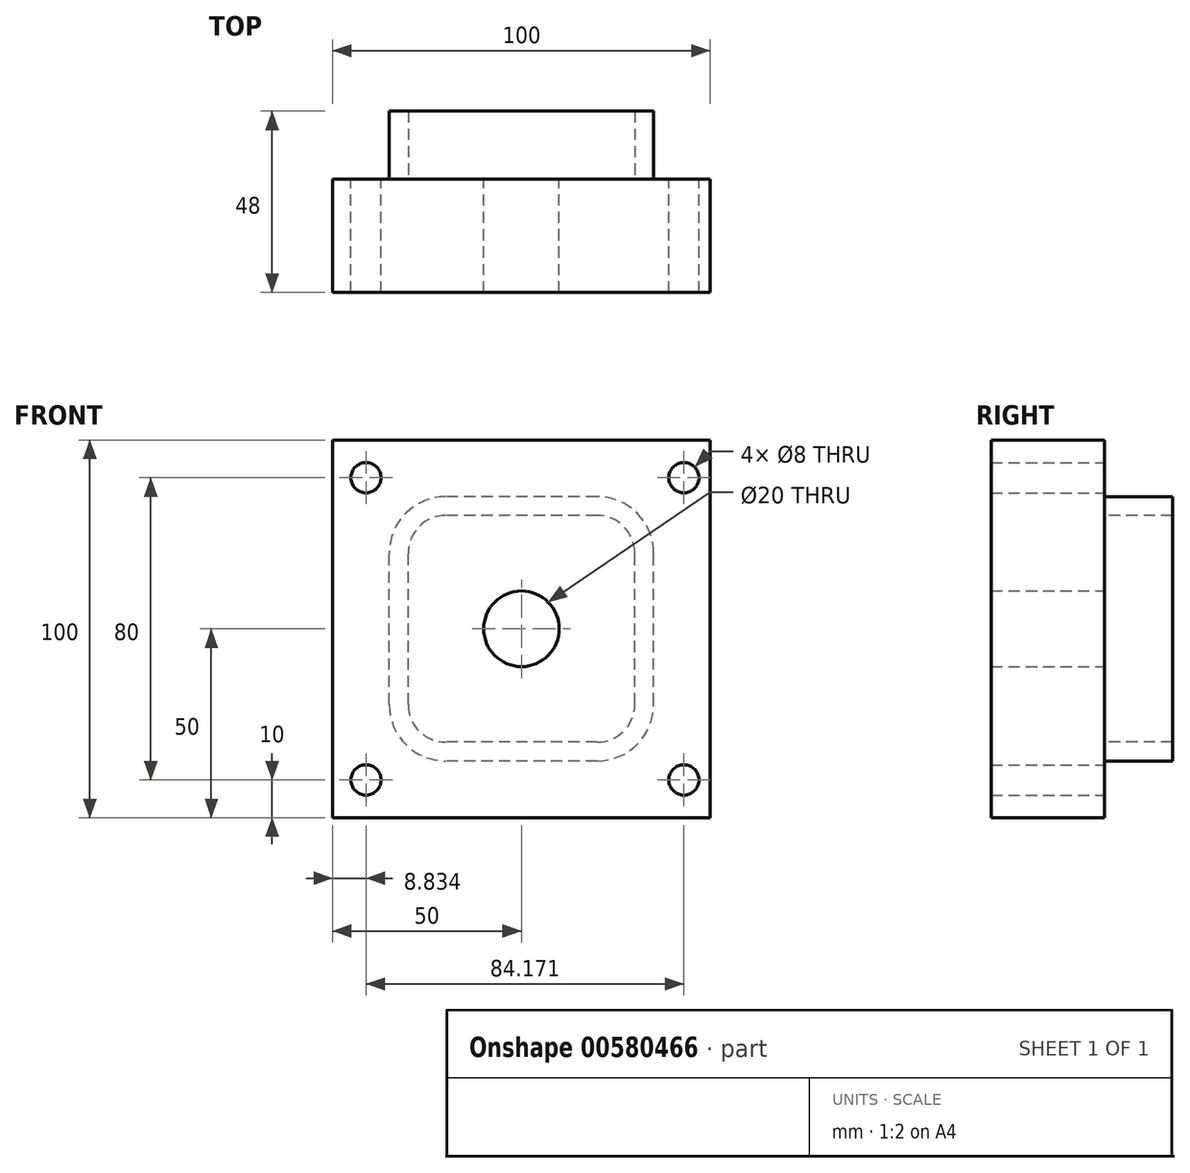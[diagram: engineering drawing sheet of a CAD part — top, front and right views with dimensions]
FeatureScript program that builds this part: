
annotation { "Feature Type Name" : "Feature", "Feature Type Description" : "" }
export const myFeature = defineFeature(function(context is Context, id is Id, definition is map)
    precondition{}
    {
        {
            var Q0;
            Q0=qCreatedBy(makeId("Front.planeOp"),FACE);
            var sketch = newSketch(context, id + "F0", { "sketchPlane" : qUnion([Q0])});
            skLineSegment(sketch, "E0.bottom", {"start": v(50, 0) * mm, "end": v(-50, 0) * mm});
            skLineSegment(sketch, "E0.top", {"start": v(50, -100) * mm, "end": v(-50, -100) * mm});
            skLineSegment(sketch, "E0.left", {"start": v(50, 0) * mm, "end": v(50, -100) * mm});
            skLineSegment(sketch, "E0.right", {"start": v(-50, 0) * mm, "end": v(-50, -100) * mm});
            skSolve(sketch);
        }
        {
            var Q0;
            Q0=makeQuery(id+"F0.imprint","IMPRINT",FACE,{"disambiguationData":[TD([[makeQuery(id+"F0.imprint","IMPRINT",EDGE,{"derivedFrom":sQuery(id+"F0.wireOp",EDGE,"E0.bottom")}),1.0]])]});
            extrude(context, id + "F1", {"entities" : qUnion([Q0]), "depth" : 30 * mm, "offsetDistance" : 25 * mm});
        }
        {
            var Q0;
            Q0=makeQuery(id+"F1.opExtrude","CAP_FACE",FACE,{"disambiguationData":[OSD([sQuery(id+"F0.wireOp",EDGE,"E0.bottom"),sQuery(id+"F0.wireOp",EDGE,"E0.top"),sQuery(id+"F0.wireOp",EDGE,"E0.left"),sQuery(id+"F0.wireOp",EDGE,"E0.right")])],"isStart":true});
            var sketch = newSketch(context, id + "F2", { "sketchPlane" : qUnion([Q0])});
            skLineSegment(sketch, "E1.bottom", {"start": v(-20, -80) * mm, "end": v(20, -80) * mm});
            skLineSegment(sketch, "E1.top", {"start": v(-20, -20) * mm, "end": v(20, -20) * mm});
            skLineSegment(sketch, "E1.left", {"start": v(-30, -70) * mm, "end": v(-30, -30) * mm});
            skLineSegment(sketch, "E1.right", {"start": v(30, -70) * mm, "end": v(30, -30) * mm});
            skArc(sketch, "E2", {"start": v(-30, -70) * mm, "mid": v(-27.07, -77.07) * mm, "end": v(-20, -80) * mm});
            skArc(sketch, "E3", {"start": v(-20, -20) * mm, "mid": v(-27.07, -22.93) * mm, "end": v(-30, -30) * mm});
            skArc(sketch, "E4", {"start": v(30, -30) * mm, "mid": v(27.07, -22.93) * mm, "end": v(20, -20) * mm});
            skArc(sketch, "E5", {"start": v(20, -80) * mm, "mid": v(27.07, -77.07) * mm, "end": v(30, -70) * mm});
            skLineSegment(sketch, "E6.bottom", {"start": v(-20, -85) * mm, "end": v(20, -85) * mm});
            skLineSegment(sketch, "E6.top", {"start": v(-20, -15) * mm, "end": v(20, -15) * mm});
            skLineSegment(sketch, "E6.left", {"start": v(-35, -70) * mm, "end": v(-35, -30) * mm});
            skLineSegment(sketch, "E6.right", {"start": v(35, -70) * mm, "end": v(35, -30) * mm});
            skArc(sketch, "E7", {"start": v(-35, -70) * mm, "mid": v(-30.6, -80.6) * mm, "end": v(-20, -85) * mm});
            skArc(sketch, "E8", {"start": v(-20, -15) * mm, "mid": v(-30.6, -19.4) * mm, "end": v(-35, -30) * mm});
            skArc(sketch, "E9", {"start": v(35, -30) * mm, "mid": v(30.6, -19.4) * mm, "end": v(20, -15) * mm});
            skArc(sketch, "E10", {"start": v(20, -85) * mm, "mid": v(30.6, -80.6) * mm, "end": v(35, -70) * mm});
            skSolve(sketch);
        }
        {
            var Q0;
            Q0=makeQuery(id+"F2.imprint","IMPRINT",FACE,{"disambiguationData":[TD([[makeQuery(id+"F2.imprint","IMPRINT",EDGE,{"derivedFrom":sQuery(id+"F2.wireOp",EDGE,"E1.bottom")}),-1.0]])]});
            extrude(context, id + "F3", {"entities" : qUnion([Q0]), "operationType" : NewBodyOperationType.ADD, "depth" : 18 * mm, "offsetDistance" : 25 * mm});
        }
        {
            var Q0;
            {var subQ0=sQuery(id+"F0.wireOp",EDGE,"E0.bottom");var subQ1=sQuery(id+"F0.wireOp",EDGE,"E0.right");var subQ2=sQuery(id+"F0.wireOp",EDGE,"E0.top");var subQ3=sQuery(id+"F0.wireOp",EDGE,"E0.left");Q0=makeQuery(id+"F3.boolean.opBoolean","SPLIT",FACE,{"disambiguationData":[TD([makeQuery(id+"F1.opExtrude","SWEPT_FACE",FACE,{"disambiguationData":[OSD([subQ0])]})])],"derivedFrom":makeQuery(id+"F1.opExtrude","CAP_FACE",FACE,{"disambiguationData":[OSD([subQ0,subQ2,subQ3,subQ1])],"isStart":true})});}
            var sketch = newSketch(context, id + "F4", { "sketchPlane" : qUnion([Q0])});
            skCircle(sketch, "E11", {"center": v(0, -50) * mm, "radius": 10 * mm});
            skCircle(sketch, "E12", {"center": v(41.17, -90) * mm, "radius": 4 * mm});
            skCircle(sketch, "E13", {"center": v(41.17, -10) * mm, "radius": 4 * mm});
            skCircle(sketch, "E14", {"center": v(-43, -90) * mm, "radius": 4 * mm});
            skCircle(sketch, "E15", {"center": v(-43, -10) * mm, "radius": 4 * mm});
            skSolve(sketch);
        }
        {
            var Q0;
            Q0 = qSketchRegion(id + "F4", true);
            extrude(context, id + "F5", {"entities" : qUnion([Q0]), "operationType" : NewBodyOperationType.REMOVE, "endBound" : BoundingType.THROUGH_ALL, "oppositeDirection" : true, "depth" : 25 * mm, "offsetDistance" : 25 * mm});
        }
    });
